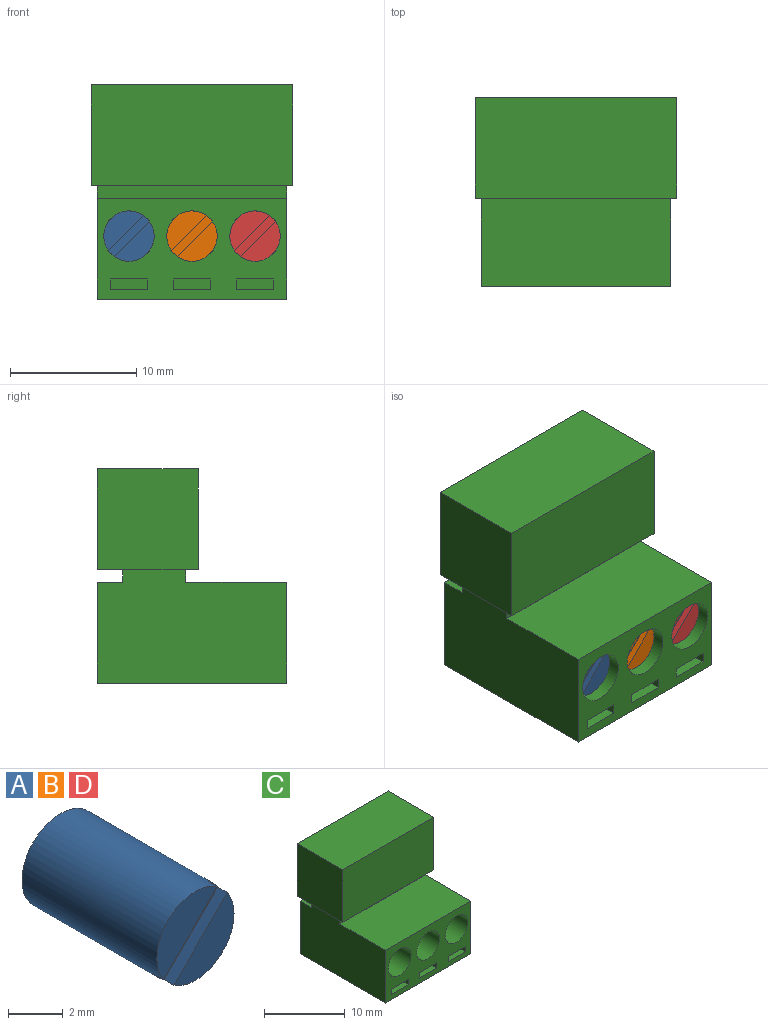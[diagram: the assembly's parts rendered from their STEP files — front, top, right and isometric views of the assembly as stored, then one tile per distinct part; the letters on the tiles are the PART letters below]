
ASSEMBLY  parts=4 mates=1
PART A: 7 faces, bbox 4x7x4 mm
  f0: cylinder r=2mm len=7mm, axis (0,1,0), area 87.2mm2, adj f1,f2,f3,f4,f5,f6
  f1: plane 3.12x3.12mm, normal (0,-1,0), area 4.8mm2, adj f0,f5
  f2: plane 3.12x3.12mm, normal (0,-1,0), area 4.8mm2, adj f0,f6
  f3: plane 4x4mm, normal (0,1,0), area 12.6mm2, adj f0
  f4: plane 3.31x3.31mm, normal (0,-1,0), area 3mm2, adj f0,f5,f6
  f5: plane 2.78x2.78mm, normal (-0.71,0,0.71), area 2mm2, adj f0,f1,f4
  f6: plane 2.78x2.78mm, normal (0.71,0,-0.71), area 2mm2, adj f0,f2,f4
PART B: same geometry as A
PART C: 63 faces, bbox 16x15x17 mm
  f0: plane 15x8mm, normal (0,-1,0), area 75.1mm2, adj f1,f2,f5,f6,f25,f27,f29,f48
  f1: plane 15x9mm, normal (1,0,0), area 125mm2, adj f0,f3,f4,f5,f6,f7,f8,f46
  f2: plane 15x9mm, normal (-1,0,0), area 125mm2, adj f0,f3,f4,f5,f6,f7,f8,f46
  f3: plane 15x1mm, normal (0,1,0), area 15mm2, adj f1,f2,f7,f46
  f4: plane 15x1mm, normal (0,-1,0), area 15mm2, adj f1,f2,f5,f46
  f5: plane 15x8mm, normal (0,0,1), area 120mm2, adj f0,f1,f2,f4
  f6: plane 15x15mm, normal (0,0,-1), area 168.8mm2, adj f0,f1,f2,f8,f30,f31,f32,f33
  f7: plane 15x2mm, normal (0,0,1), area 30mm2, adj f1,f2,f3,f8
  f8: plane 15x8mm, normal (0,1,0), area 120mm2, adj f1,f2,f6,f7
  f9: plane 3.2x3mm, normal (0,0,-1), area 9.6mm2, adj f10,f11,f12,f13
  f10: plane 7x3.2mm, normal (-1,0,0), area 22.4mm2, adj f9,f11,f12,f38
  f11: plane 7x3mm, normal (0,-1,0), area 21mm2, adj f9,f10,f13,f32
  f12: plane 7x3mm, normal (0,1,0), area 21mm2, adj f9,f10,f13,f33
  f13: plane 7x3.2mm, normal (1,0,0), area 22.4mm2, adj f9,f11,f12,f39
  f14: plane 3.2x3mm, normal (0,0,-1), area 9.6mm2, adj f15,f16,f17,f18
  f15: plane 7x3.2mm, normal (-1,0,0), area 22.4mm2, adj f14,f16,f17,f40
  f16: plane 7x3mm, normal (0,-1,0), area 21mm2, adj f14,f15,f18,f35
  f17: plane 7x3mm, normal (0,1,0), area 21mm2, adj f14,f15,f18,f34
  f18: plane 7x3.2mm, normal (1,0,0), area 22.4mm2, adj f14,f16,f17,f41
  f19: plane 3.2x3mm, normal (0,0,-1), area 9.6mm2, adj f20,f21,f22,f23
  f20: plane 7x3mm, normal (0,-1,0), area 21mm2, adj f19,f21,f22,f30
  f21: plane 7x3.2mm, normal (1,0,0), area 22.4mm2, adj f19,f20,f23,f37
  f22: plane 7x3.2mm, normal (-1,0,0), area 22.4mm2, adj f19,f20,f23,f36
  f23: plane 7x3mm, normal (0,1,0), area 21mm2, adj f19,f21,f22,f31
  f24: plane 4x4mm, normal (0,-1,0), area 12.6mm2, adj f25
  f25: cylinder r=2mm len=8mm, axis (0,-1,0), area 100.5mm2, adj f0,f24
  f26: plane 4x4mm, normal (0,-1,0), area 12.6mm2, adj f27
  f27: cylinder r=2mm len=8mm, axis (0,-1,0), area 100.5mm2, adj f0,f26
  f28: plane 4x4mm, normal (0,-1,0), area 12.6mm2, adj f29
  f29: cylinder r=2mm len=8mm, axis (0,-1,0), area 100.5mm2, adj f0,f28
  f30: plane 3.6x1mm, normal (0,-0.71,-0.71), area 4.7mm2, adj f6,f20,f36,f37
  f31: plane 3.6x1mm, normal (0,0.71,-0.71), area 4.7mm2, adj f6,f23,f36,f37
  f32: plane 3.6x1mm, normal (0,-0.71,-0.71), area 4.7mm2, adj f6,f11,f38,f39
  f33: plane 3.6x1mm, normal (0,0.71,-0.71), area 4.7mm2, adj f6,f12,f38,f39
  f34: plane 3.6x1mm, normal (0,0.71,-0.71), area 4.7mm2, adj f6,f17,f40,f41
  f35: plane 3.6x1mm, normal (0,-0.71,-0.71), area 4.7mm2, adj f6,f16,f40,f41
  f36: plane 5.2x1mm, normal (-0.96,0,-0.29), area 4.4mm2, adj f6,f22,f30,f31
  f37: plane 5.2x1mm, normal (0.96,0,-0.29), area 4.4mm2, adj f6,f21,f30,f31
  f38: plane 5.2x1mm, normal (-0.96,0,-0.29), area 4.4mm2, adj f6,f10,f32,f33
  f39: plane 5.2x1mm, normal (0.96,0,-0.29), area 4.4mm2, adj f6,f13,f32,f33
  f40: plane 5.2x1mm, normal (-0.96,0,-0.29), area 4.4mm2, adj f6,f15,f34,f35
  f41: plane 5.2x1mm, normal (0.96,0,-0.29), area 4.4mm2, adj f6,f18,f34,f35
  f42: plane 16x8mm, normal (0,-1,0), area 128mm2, adj f43,f45,f46,f47
  f43: plane 8x8mm, normal (1,0,0), area 64mm2, adj f42,f44,f46,f47
  f44: plane 16x8mm, normal (0,1,0), area 128mm2, adj f43,f45,f46,f47
  f45: plane 8x8mm, normal (-1,0,0), area 64mm2, adj f42,f44,f46,f47
  f46: plane 16x8mm, normal (0,0,-1), area 53mm2, adj f1,f2,f3,f4,f42,f43,f44,f45
  f47: plane 16x8mm, normal (0,0,1), area 128mm2, adj f42,f43,f44,f45
  f48: plane 3x2mm, normal (0,0,-1), area 6mm2, adj f0,f49,f51,f52
  f49: plane 2x0.8mm, normal (1,0,0), area 1.6mm2, adj f0,f48,f50,f52
  f50: plane 3x2mm, normal (0,0,1), area 6mm2, adj f0,f49,f51,f52
  f51: plane 2x0.8mm, normal (-1,0,0), area 1.6mm2, adj f0,f48,f50,f52
  f52: plane 3x0.8mm, normal (0,-1,0), area 2.4mm2, adj f48,f49,f50,f51
  f53: plane 3x2mm, normal (0,0,-1), area 6mm2, adj f0,f54,f56,f57
  f54: plane 2x0.8mm, normal (1,0,0), area 1.6mm2, adj f0,f53,f55,f57
  f55: plane 3x2mm, normal (0,0,1), area 6mm2, adj f0,f54,f56,f57
  f56: plane 2x0.8mm, normal (-1,0,0), area 1.6mm2, adj f0,f53,f55,f57
  f57: plane 3x0.8mm, normal (0,-1,0), area 2.4mm2, adj f53,f54,f55,f56
  f58: plane 3x2mm, normal (0,0,1), area 6mm2, adj f0,f59,f61,f62
  f59: plane 2x0.8mm, normal (-1,0,0), area 1.6mm2, adj f0,f58,f60,f62
  f60: plane 3x2mm, normal (0,0,-1), area 6mm2, adj f0,f59,f61,f62
  f61: plane 2x0.8mm, normal (1,0,0), area 1.6mm2, adj f0,f58,f60,f62
  f62: plane 3x0.8mm, normal (0,-1,0), area 2.4mm2, adj f58,f59,f60,f61
PART D: same geometry as A
PLACE A t=(-15.86,-6.59,-3.23)mm
PLACE B t=(-10.86,-6.59,-3.23)mm
PLACE C t=(-10.86,0.41,-4.23)mm
PLACE D t=(-5.86,-6.59,-3.23)mm
MATE fastened A.f0 <-> C.f27  axis (0,1,0) through (-15.86,-6.59,-3.23)mm
